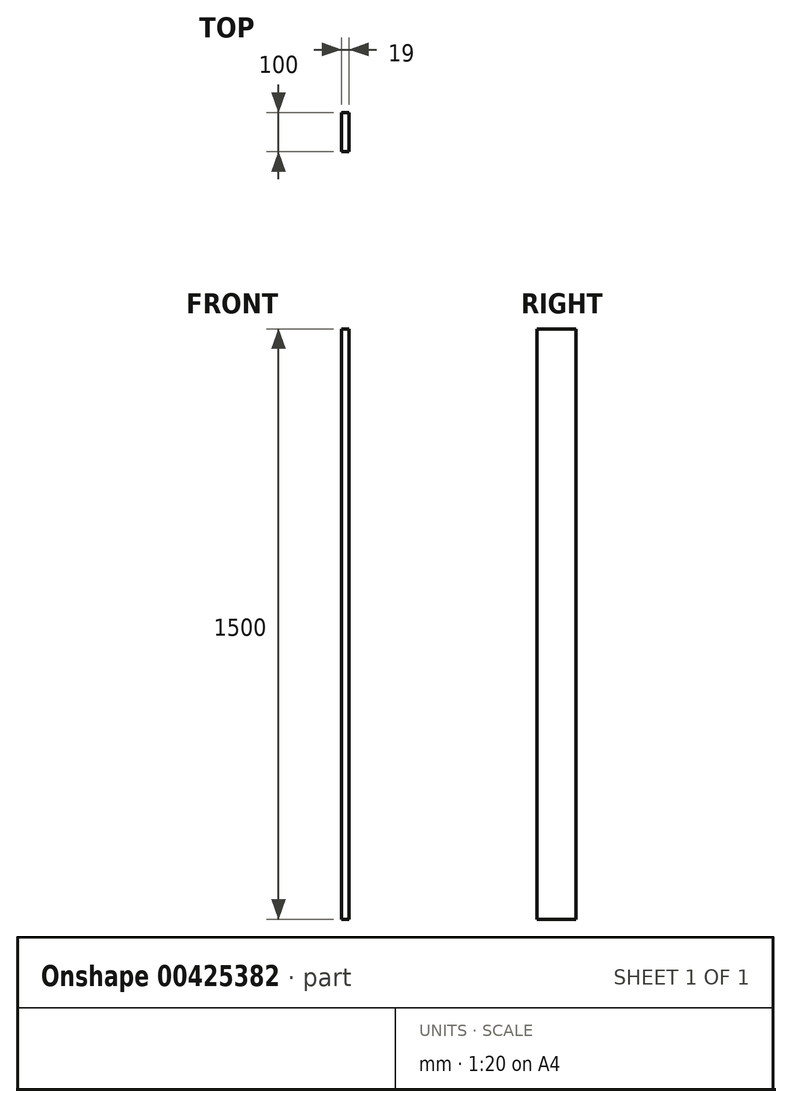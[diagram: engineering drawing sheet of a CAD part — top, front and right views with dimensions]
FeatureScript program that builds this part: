
annotation { "Feature Type Name" : "Feature", "Feature Type Description" : "" }
export const myFeature = defineFeature(function(context is Context, id is Id, definition is map)
    precondition{}
    {
        {
            var Q0;
            Q0=qCreatedBy(makeId("Top.planeOp"),FACE);
            var sketch = newSketch(context, id + "F0", { "sketchPlane" : qUnion([Q0])});
            skLineSegment(sketch, "E0.bottom", {"start": v(-4.74, 55.5) * mm, "end": v(-23.74, 55.5) * mm});
            skLineSegment(sketch, "E0.top", {"start": v(-4.74, -44.5) * mm, "end": v(-23.74, -44.5) * mm});
            skLineSegment(sketch, "E0.left", {"start": v(-4.74, 55.5) * mm, "end": v(-4.74, -44.5) * mm});
            skLineSegment(sketch, "E0.right", {"start": v(-23.74, 55.5) * mm, "end": v(-23.74, -44.5) * mm});
            skSolve(sketch);
        }
        {
            var Q0;
            Q0=makeQuery(id+"F0.imprint","IMPRINT",FACE,{"disambiguationData":[TD([[makeQuery(id+"F0.imprint","IMPRINT",EDGE,{"derivedFrom":sQuery(id+"F0.wireOp",EDGE,"E0.bottom")}),1.0]])]});
            extrude(context, id + "F1", {"entities" : qUnion([Q0]), "depth" : 1500 * mm});
        }
    });
